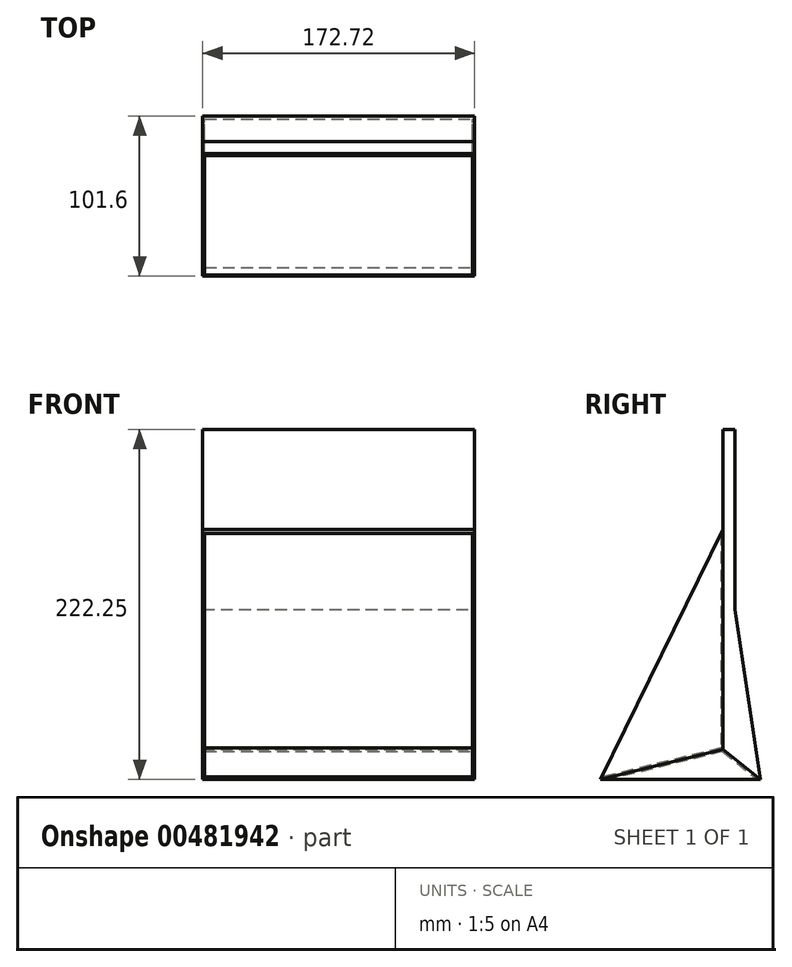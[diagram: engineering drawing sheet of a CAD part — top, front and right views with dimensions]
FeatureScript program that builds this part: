
annotation { "Feature Type Name" : "Feature", "Feature Type Description" : "" }
export const myFeature = defineFeature(function(context is Context, id is Id, definition is map)
    precondition{}
    {
        {
            var Q0;
            Q0=qCreatedBy(makeId("Right.planeOp"),FACE);
            var sketch = newSketch(context, id + "F0", { "sketchPlane" : qUnion([Q0])});
            skLineSegment(sketch, "E0", {"start": v(0, 0) * mm, "end": v(101.6, 0) * mm});
            skLineSegment(sketch, "E1", {"start": v(101.6, 0) * mm, "end": v(77.72, 158.75) * mm});
            skLineSegment(sketch, "E2", {"start": v(77.72, 158.75) * mm, "end": v(0, 0) * mm});
            skLineSegment(sketch, "E3", {"start": v(77.72, 158.75) * mm, "end": v(77.72, 19.05) * mm});
            skLineSegment(sketch, "E4", {"start": v(77.72, 19.05) * mm, "end": v(101.6, 0) * mm});
            skLineSegment(sketch, "E5", {"start": v(77.72, 19.05) * mm, "end": v(0, 0) * mm});
            skLineSegment(sketch, "E6", {"start": v(77.72, 158.75) * mm, "end": v(77.72, 222.25) * mm});
            skLineSegment(sketch, "E7", {"start": v(77.72, 222.25) * mm, "end": v(85.34, 222.25) * mm});
            skLineSegment(sketch, "E8", {"start": v(85.34, 222.25) * mm, "end": v(85.34, 108.09) * mm});
            skSolve(sketch);
        }
        {
            var Q0;
            Q0=makeQuery(id+"F0.imprint","IMPRINT",FACE,{"disambiguationData":[TD([[makeQuery(id+"F0.imprint","IMPRINT",EDGE,{"derivedFrom":sQuery(id+"F0.wireOp",EDGE,"E2")}),1.0]])]});
            extrude(context, id + "F1", {"entities" : qUnion([Q0]), "oppositeDirection" : true, "depth" : 172.72 * mm, "offsetDistance" : 25.4 * mm});
        }
        {
            var Q0;
            {var subQ3=sQuery(id+"F0.wireOp",EDGE,"E3");Q0=makeQuery(id+"F0.imprint","IMPRINT",FACE,{"disambiguationData":[TD([[makeQuery(id+"F0.imprint","IMPRINT",EDGE,{"derivedFrom":subQ3}),1.0]])]});}
            var Q1;
            {var subQ0=sQuery(id+"F0.wireOp",EDGE,"E6");Q1=makeQuery(id+"F0.imprint","IMPRINT",FACE,{"disambiguationData":[TD([[makeQuery(id+"F0.imprint","IMPRINT",EDGE,{"derivedFrom":subQ0}),-1.0]])]});}
            extrude(context, id + "F2", {"entities" : qUnion([Q0, Q1]), "oppositeDirection" : true, "depth" : 172.72 * mm, "offsetDistance" : 25.4 * mm});
        }
        {
            var Q0;
            Q0=makeQuery(id+"F0.imprint","IMPRINT",FACE,{"disambiguationData":[TD([[makeQuery(id+"F0.imprint","IMPRINT",EDGE,{"derivedFrom":sQuery(id+"F0.wireOp",EDGE,"E0")}),1.0]])]});
            extrude(context, id + "F3", {"entities" : qUnion([Q0]), "oppositeDirection" : true, "depth" : 172.72 * mm, "offsetDistance" : 25.4 * mm});
        }
        {
            var Q0;
            Q0=makeQuery(id+"F1.opExtrude","SWEPT_FACE",FACE,{"disambiguationData":[OSD([sQuery(id+"F0.wireOp",EDGE,"E2")])]});
            shell(context, id + "F4", {"entities" : qUnion([Q0]), "thickness" : 1.27 * mm});
        }
        {
            var Q0;
            Q0=makeQuery(id+"F3.opExtrude","SWEPT_FACE",FACE,{"disambiguationData":[OSD([sQuery(id+"F0.wireOp",EDGE,"E0")])]});
            shell(context, id + "F5", {"entities" : qUnion([Q0]), "thickness" : 1.27 * mm});
        }
    });
